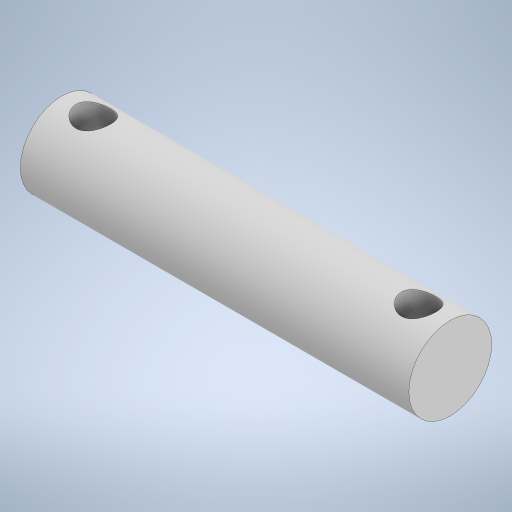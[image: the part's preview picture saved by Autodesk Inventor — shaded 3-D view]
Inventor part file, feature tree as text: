
AUTODESK INVENTOR PART (.ipt)
format: ipt  version: 2023 (Build 270158000, 158)  size: 244,224 bytes
history: native  units: in
note: dims shown in document units (in); Inventor stores cm internally (conversion verified against a paired STEP export)
features: extrude x2, sketch x2, plane x1
ambient origin geometry x8: Origin, YZ Plane, XZ Plane, XY Plane, X Axis, Y Axis, Z Axis, Center Point
bodies: Solid1 (feature_tree)
feature tree (5):
  extrude  "Extrusion1"  Depth=1.125in TaperAngle=0.0deg
  plane  "Work Plane1"
  extrude  "Extrusion2"  Depth=0.471in
  sketch  "Sketch1"  dims[d0=0.24in d1=1.125in d2=0.0in]
  sketch  "Sketch2"  dims[d3=0.1875in d4=0.471in d5=0.471in d6=0.1in d7=1.0in d8=0.0in d9=0.1in]
